# Revit family: 756-106-681-DN700-2800
name_source: partatom
category: Pipe Accessories
units: mm (PartAtom-declared; Revit-internal decimal feet)

## family parameters
Always vertical = Yes
Cut with Voids When Loaded = No
Part Type = Valve - Breaks Into
Round Connector Dimension = Use Diameter
Shared = No
Work Plane-Based = No

## types (27) — shared parameters
Body_wallthickness = 10 mm  [stored 0.0328084 ft]
DN0700_PN10 = 756-0700-1-04006
DN0700_PN16 = 756-0700-1-14006
DN0800_PN10 = 756-0800-1-04006
DN0800_PN16 = 756-0800-1-14006
DN0900_PN10 = 756-0900-1-04006
DN0900_PN16 = 756-0900-1-14006
DN1000 = Yes
DN1000_PN10 = 756-1000-1-04006
DN1000_PN16 = 756-1000-1-14006
DN1200 = Yes
DN1200_PN10 = 756-1200-1-04006
DN1200_PN16 = 756-1200-1-14006
DN1400 = Yes
DN1400_PN10 = 756-1400-1-04006
DN1400_PN16 = 756-1400-1-14006
DN1500 = Yes
DN1500_PN10 = 756-1500-1-04006
DN1500_PN16 = 756-1500-1-14006
DN1600 = Yes
DN1600_PN10 = 756-1600-1-04006
DN1600_PN16 = 756-1600-1-14006
DN1800 = Yes
DN1800_PN10 = 756-1800-1-04006
DN1800_PN16 = 756-1800-1-14006
DN2000 = Yes
DN2000_PN10 = 756-2000-1-04006
DN2000_PN16 = 756-2000-1-14006
DN2200 = Yes
DN2200_PN10_DIN = 756-2200-1-04006
DN2200_PN16_DIN = 756-2200-1-14006
DN2400 = Yes
DN2400_PN10_DIN = 756-2400-1-04006
DN2400_PN16_DIN = 756-2400-1-14006
DN2600 = Yes
DN2600_PN10 = 756-2600-1-04006
DN2600_PN16 = 756-2600-1-14006
DN2800 = Yes
DN2800_PN10 = 756-2800-1-04006
DN700 = Yes
DN800 = Yes
DN900 = Yes
Description_ = AVK_DOUBLE_ECCENTRIC_BUTTERFLY_VALVE
HW_rod_Dia = 30 mm  [stored 0.0984252 ft]
Offset = 3 mm  [stored 0.00984252 ft]
Pin_dia = 60 mm  [stored 0.19685 ft]
RF_Cut_Thickness = 5 mm  [stored 0.0164042 ft]
Rib_depth = 15 mm  [stored 0.0492126 ft]
Search_table = 756-106-681-DN700-2800
URL_product_pages = https://www.avkvalves.com

## per-type parameters (varying)
- DN0700_PN10: Bottom_Depth=1050 mm; Bottom_width=395 mm; CD_rod=39 mm  [stored 0.127953 ft]; D=285 mm; DN=700 mm; Disc_Dia=689 mm; Disc_width=40 mm  [stored 0.131234 ft]; Disk_1=40 mm  [stored 0.131234 ft]; Disk_2=40 mm  [stored 0.131234 ft]; Flange_OD=448 mm; Flange_Thickness=40 mm  [stored 0.131234 ft]; Gear_box_Mount_Flange_thickness=30 mm  [stored 0.0984252 ft]; Gear_box_Mount_Flange_width=102 mm; Gear_box_Mount_width=62 mm  [stored 0.203412 ft]; Gear_box_width=133 mm; H1=497 mm; H2=550 mm; HW_Connecting_Rib=570 mm; HW_Connecting_Rib_ref=569 mm; HW_Ref=110 mm; HW_height=381 mm; Hand_wheel_rod=33 mm  [stored 0.108268 ft]; ID (Radius)=350 mm; L=430 mm; L1=127 mm; L2=133 mm; Pin_Depth=798 mm; Pin_width=215 mm; Rf_Dia=397 mm; Rib_height=407 mm; Rib_height_2=50 mm  [stored 0.164042 ft]; Rib_width=350 mm; Rib_width_2=204 mm; W1=448 mm; W2=641 mm; W3=533 mm; W4=543 mm; W5=396 mm
- DN0700_PN16: Bottom_Depth=1050 mm; Bottom_width=427 mm; CD_rod=39 mm  [stored 0.127953 ft]; D=335 mm; DN=700 mm; Disc_Dia=689 mm; Disc_width=40 mm  [stored 0.131234 ft]; Disk_1=40 mm  [stored 0.131234 ft]; Disk_2=40 mm  [stored 0.131234 ft]; Flange_OD=455 mm; Flange_Thickness=40 mm  [stored 0.131234 ft]; Gear_box_Mount_Flange_thickness=30 mm  [stored 0.0984252 ft]; Gear_box_Mount_Flange_width=107 mm; Gear_box_Mount_width=66 mm  [stored 0.216535 ft]; Gear_box_width=139 mm; H1=532 mm; H2=550 mm; HW_Connecting_Rib=670 mm; HW_Connecting_Rib_ref=587 mm; HW_Ref=110 mm; HW_height=502 mm; Hand_wheel_rod=35 mm; ID (Radius)=350 mm; L=430 mm; L1=127 mm; L2=133 mm; Pin_Depth=805 mm; Pin_width=215 mm; Rf_Dia=397 mm; Rib_height=414 mm; Rib_height_2=77 mm  [stored 0.252625 ft]; Rib_width=350 mm; Rib_width_2=214 mm; W1=455 mm; W2=641 mm; W3=533 mm; W4=543 mm; W5=517 mm
- DN0800_PN10: Bottom_Depth=1200 mm; Bottom_width=460 mm; CD_rod=39 mm  [stored 0.127953 ft]; D=285 mm; DN=800 mm; Disc_Dia=788 mm; Disc_width=40 mm  [stored 0.131234 ft]; Disk_1=40 mm  [stored 0.131234 ft]; Disk_2=40 mm  [stored 0.131234 ft]; Flange_OD=508 mm; Flange_Thickness=40 mm  [stored 0.131234 ft]; Gear_box_Mount_Flange_thickness=40 mm  [stored 0.131234 ft]; Gear_box_Mount_Flange_width=112 mm; Gear_box_Mount_width=68 mm  [stored 0.223097 ft]; Gear_box_width=145 mm; H1=603 mm; H2=620 mm; HW_Connecting_Rib=570 mm; HW_Connecting_Rib_ref=657 mm; HW_Ref=125 mm; HW_height=381 mm; Hand_wheel_rod=36 mm  [stored 0.11811 ft]; ID (Radius)=400 mm; L=470 mm; L1=156 mm; L2=162 mm; Pin_Depth=908 mm; Pin_width=235 mm; Rf_Dia=450 mm; Rib_height=461 mm; Rib_height_2=96 mm; Rib_width=390 mm; Rib_width_2=223 mm; W1=508 mm; W2=711 mm; W3=627 mm; W4=636 mm; W5=396 mm
- DN0800_PN16: Bottom_Depth=1200 mm; Bottom_width=492 mm; CD_rod=39 mm  [stored 0.127953 ft]; D=335 mm; DN=800 mm; Disc_Dia=788 mm; Disc_width=40 mm  [stored 0.131234 ft]; Disk_1=40 mm  [stored 0.131234 ft]; Disk_2=40 mm  [stored 0.131234 ft]; Flange_OD=513 mm; Flange_Thickness=40 mm  [stored 0.131234 ft]; Gear_box_Mount_Flange_thickness=40 mm  [stored 0.131234 ft]; Gear_box_Mount_Flange_width=116 mm; Gear_box_Mount_width=72 mm  [stored 0.23622 ft]; Gear_box_width=151 mm; H1=603 mm; H2=620 mm; HW_Connecting_Rib=670 mm; HW_Connecting_Rib_ref=657 mm; HW_Ref=125 mm; HW_height=502 mm; Hand_wheel_rod=38 mm  [stored 0.124672 ft]; ID (Radius)=400 mm; L=470 mm; L1=156 mm; L2=162 mm; Pin_Depth=913 mm; Pin_width=235 mm; Rf_Dia=450 mm; Rib_height=466 mm; Rib_height_2=91 mm; Rib_width=390 mm; Rib_width_2=232 mm; W1=513 mm; W2=711 mm; W3=627 mm; W4=636 mm; W5=517 mm
- DN0900_PN10: Bottom_Depth=1350 mm; Bottom_width=524 mm; CD_rod=39 mm  [stored 0.127953 ft]; D=335 mm; DN=900 mm; Disc_Dia=888 mm; Disc_width=40 mm  [stored 0.131234 ft]; Disk_1=40 mm  [stored 0.131234 ft]; Disk_2=40 mm  [stored 0.131234 ft]; Flange_OD=558 mm; Flange_Thickness=40 mm  [stored 0.131234 ft]; Gear_box_Mount_Flange_thickness=40 mm  [stored 0.131234 ft]; Gear_box_Mount_Flange_width=121 mm; Gear_box_Mount_width=74 mm  [stored 0.242782 ft]; Gear_box_width=157 mm; H1=674 mm; H2=690 mm; HW_Connecting_Rib=670 mm; HW_Connecting_Rib_ref=733 mm; HW_Ref=128 mm; HW_height=502 mm; Hand_wheel_rod=39 mm  [stored 0.127953 ft]; ID (Radius)=450 mm; L=510 mm; L1=186 mm; L2=192 mm; Pin_Depth=1008 mm; Pin_width=255 mm; Rf_Dia=500 mm; Rib_height=507 mm; Rib_height_2=117 mm; Rib_width=430 mm; Rib_width_2=241 mm; W1=558 mm; W2=791 mm; W3=722 mm; W4=730 mm; W5=517 mm
- DN0900_PN16: Bottom_Depth=1350 mm; Bottom_width=556 mm; CD_rod=39 mm  [stored 0.127953 ft]; D=335 mm; DN=900 mm; Disc_Dia=888 mm; Disc_width=40 mm  [stored 0.131234 ft]; Disk_1=40 mm  [stored 0.131234 ft]; Disk_2=40 mm  [stored 0.131234 ft]; Flange_OD=563 mm; Flange_Thickness=40 mm  [stored 0.131234 ft]; Gear_box_Mount_Flange_thickness=40 mm  [stored 0.131234 ft]; Gear_box_Mount_Flange_width=125 mm; Gear_box_Mount_width=76 mm  [stored 0.249344 ft]; Gear_box_width=163 mm; H1=674 mm; H2=690 mm; HW_Connecting_Rib=670 mm; HW_Connecting_Rib_ref=733 mm; HW_Ref=128 mm; HW_height=555 mm; Hand_wheel_rod=41 mm  [stored 0.134514 ft]; ID (Radius)=450 mm; L=510 mm; L1=186 mm; L2=192 mm; Pin_Depth=1013 mm; Pin_width=255 mm; Rf_Dia=500 mm; Rib_height=511 mm; Rib_height_2=112 mm; Rib_width=430 mm; Rib_width_2=250 mm; W1=563 mm; W2=791 mm; W3=722 mm; W4=730 mm; W5=570 mm
- DN1000_PN10: Bottom_Depth=1500 mm; Bottom_width=588 mm; CD_rod=49 mm  [stored 0.160761 ft]; D=335 mm; DN=1000 mm; Disc_Dia=987 mm; Disc_width=50 mm  [stored 0.164042 ft]; Disk_1=40 mm  [stored 0.131234 ft]; Disk_2=40 mm  [stored 0.131234 ft]; Flange_OD=615 mm; Flange_Thickness=40 mm  [stored 0.131234 ft]; Gear_box_Mount_Flange_thickness=40 mm  [stored 0.131234 ft]; Gear_box_Mount_Flange_width=130 mm; Gear_box_Mount_width=80 mm; Gear_box_width=168 mm; H1=745 mm; H2=770 mm; HW_Connecting_Rib=670 mm; HW_Connecting_Rib_ref=808 mm; HW_Ref=130 mm; HW_height=515 mm; Hand_wheel_rod=42 mm  [stored 0.137795 ft]; ID (Radius)=500 mm; L=550 mm; L1=216 mm; L2=222 mm; Pin_Depth=1115 mm; Pin_width=275 mm; Rf_Dia=556 mm; Rib_height=559 mm; Rib_height_2=130 mm; Rib_width=470 mm; Rib_width_2=259 mm; W1=615 mm; W2=871 mm; W3=816 mm; W4=824 mm; W5=530 mm
- DN1000_PN16: Bottom_Depth=1500 mm; Bottom_width=620 mm; CD_rod=49 mm  [stored 0.160761 ft]; D=285 mm; DN=1000 mm; Disc_Dia=987 mm; Disc_width=50 mm  [stored 0.164042 ft]; Disk_1=50 mm  [stored 0.164042 ft]; Disk_2=50 mm  [stored 0.164042 ft]; Flange_OD=628 mm; Flange_Thickness=40 mm  [stored 0.131234 ft]; Gear_box_Mount_Flange_thickness=40 mm  [stored 0.131234 ft]; Gear_box_Mount_Flange_width=134 mm; Gear_box_Mount_width=82 mm; Gear_box_width=174 mm; H1=745 mm; H2=770 mm; HW_Connecting_Rib=570 mm; HW_Connecting_Rib_ref=808 mm; HW_Ref=130 mm; HW_height=555 mm; Hand_wheel_rod=44 mm; ID (Radius)=500 mm; L=550 mm; L1=216 mm; L2=222 mm; Pin_Depth=1128 mm; Pin_width=275 mm; Rf_Dia=556 mm; Rib_height=570 mm; Rib_height_2=118 mm; Rib_width=470 mm; Rib_width_2=268 mm; W1=628 mm; W2=871 mm; W3=816 mm; W4=824 mm; W5=570 mm
- DN1200_PN10: Bottom_Depth=1800 mm; Bottom_width=653 mm; CD_rod=49 mm  [stored 0.160761 ft]; D=285 mm; DN=1200 mm; Disc_Dia=1174 mm; Disc_width=50 mm  [stored 0.164042 ft]; Disk_1=50 mm  [stored 0.164042 ft]; Disk_2=50 mm  [stored 0.164042 ft]; Flange_OD=728 mm; Flange_Thickness=40 mm  [stored 0.131234 ft]; Gear_box_Mount_Flange_thickness=40 mm  [stored 0.131234 ft]; Gear_box_Mount_Flange_width=139 mm; Gear_box_Mount_width=84 mm; Gear_box_width=180 mm; H1=840 mm; H2=855 mm; HW_Connecting_Rib=570 mm; HW_Connecting_Rib_ref=898 mm; HW_Ref=128 mm; HW_height=555 mm; Hand_wheel_rod=45 mm  [stored 0.147638 ft]; ID (Radius)=600 mm; L=630 mm; L1=269 mm; L2=275 mm; Pin_Depth=1328 mm; Pin_width=315 mm; Rf_Dia=666 mm; Rib_height=661 mm; Rib_height_2=113 mm; Rib_width=550 mm; Rib_width_2=277 mm; W1=728 mm; W2=956 mm; W3=986 mm; W4=993 mm; W5=570 mm
- DN1200_PN16: Bottom_Depth=1800 mm; Bottom_width=685 mm; CD_rod=49 mm  [stored 0.160761 ft]; D=335 mm; DN=1200 mm; Disc_Dia=1174 mm; Disc_width=50 mm  [stored 0.164042 ft]; Disk_1=50 mm  [stored 0.164042 ft]; Disk_2=50 mm  [stored 0.164042 ft]; Flange_OD=743 mm; Flange_Thickness=50 mm  [stored 0.164042 ft]; Gear_box_Mount_Flange_thickness=40 mm  [stored 0.131234 ft]; Gear_box_Mount_Flange_width=143 mm; Gear_box_Mount_width=88 mm; Gear_box_width=186 mm; H1=840 mm; H2=855 mm; HW_Connecting_Rib=670 mm; HW_Connecting_Rib_ref=898 mm; HW_Ref=128 mm; HW_height=576 mm; Hand_wheel_rod=47 mm  [stored 0.154199 ft]; ID (Radius)=600 mm; L=630 mm; L1=269 mm; L2=275 mm; Pin_Depth=1343 mm; Pin_width=315 mm; Rf_Dia=666 mm; Rib_height=675 mm; Rib_height_2=98 mm; Rib_width=530 mm; Rib_width_2=286 mm; W1=743 mm; W2=956 mm; W3=986 mm; W4=993 mm; W5=591 mm
- DN1400_PN10: Bottom_Depth=2100 mm; Bottom_width=717 mm; CD_rod=59 mm  [stored 0.19357 ft]; D=335 mm; DN=1400 mm; Disc_Dia=1381 mm; Disc_width=60 mm  [stored 0.19685 ft]; Disk_1=50 mm  [stored 0.164042 ft]; Disk_2=50 mm  [stored 0.164042 ft]; Flange_OD=838 mm; Flange_Thickness=50 mm  [stored 0.164042 ft]; Gear_box_Mount_Flange_thickness=40 mm  [stored 0.131234 ft]; Gear_box_Mount_Flange_width=148 mm; Gear_box_Mount_width=90 mm; Gear_box_width=192 mm; H1=920 mm; H2=970 mm; HW_Connecting_Rib=670 mm; HW_Connecting_Rib_ref=996 mm; HW_Ref=150 mm; HW_height=555 mm; Hand_wheel_rod=48 mm  [stored 0.15748 ft]; ID (Radius)=700 mm; L=710 mm; L1=333 mm; L2=339 mm; Pin_Depth=1538 mm; Pin_width=355 mm; Rf_Dia=763 mm; Rib_height=761 mm; Rib_height_2=83 mm; Rib_width=610 mm; Rib_width_2=295 mm; W1=838 mm; W2=1071 mm; W3=1182 mm; W4=1189 mm; W5=570 mm
- DN1400_PN16: Bottom_Depth=2100 mm; Bottom_width=749 mm; CD_rod=59 mm  [stored 0.19357 ft]; D=335 mm; DN=1400 mm; Disc_Dia=1381 mm; Disc_width=60 mm  [stored 0.19685 ft]; Disk_1=50 mm  [stored 0.164042 ft]; Disk_2=50 mm  [stored 0.164042 ft]; Flange_OD=843 mm; Flange_Thickness=50 mm  [stored 0.164042 ft]; Gear_box_Mount_Flange_thickness=40 mm  [stored 0.131234 ft]; Gear_box_Mount_Flange_width=152 mm; Gear_box_Mount_width=94 mm; Gear_box_width=198 mm; H1=920 mm; H2=970 mm; HW_Connecting_Rib=670 mm; HW_Connecting_Rib_ref=1020 mm; HW_Ref=150 mm; HW_height=576 mm; Hand_wheel_rod=50 mm  [stored 0.164042 ft]; ID (Radius)=700 mm; L=710 mm; L1=333 mm; L2=339 mm; Pin_Depth=1543 mm; Pin_width=355 mm; Rf_Dia=763 mm; Rib_height=766 mm; Rib_height_2=78 mm; Rib_width=610 mm; Rib_width_2=304 mm; W1=843 mm; W2=1119 mm; W3=1182 mm; W4=1189 mm; W5=591 mm
- DN1500_PN10: Bottom_Depth=2250 mm; Bottom_width=781 mm; CD_rod=59 mm  [stored 0.19357 ft]; D=335 mm; DN=1500 mm; Disc_Dia=1481 mm; Disc_width=60 mm  [stored 0.19685 ft]; Disk_1=50 mm  [stored 0.164042 ft]; Disk_2=50 mm  [stored 0.164042 ft]; Flange_OD=893 mm; Flange_Thickness=50 mm  [stored 0.164042 ft]; Gear_box_Mount_Flange_thickness=40 mm  [stored 0.131234 ft]; Gear_box_Mount_Flange_width=157 mm; Gear_box_Mount_width=96 mm; Gear_box_width=203 mm; H1=1000 mm; H2=1070 mm; HW_Connecting_Rib=670 mm; HW_Connecting_Rib_ref=1086 mm; HW_Ref=175 mm; HW_height=555 mm; Hand_wheel_rod=51 mm  [stored 0.167323 ft]; ID (Radius)=750 mm; L=750 mm; L1=363 mm; L2=369 mm; Pin_Depth=1643 mm; Pin_width=375 mm; Rf_Dia=818 mm; Rib_height=811 mm; Rib_height_2=108 mm; Rib_width=650 mm; Rib_width_2=313 mm; W1=893 mm; W2=1171 mm; W3=1274 mm; W4=1281 mm; W5=570 mm
- DN1500_PN16: Bottom_Depth=2250 mm; Bottom_width=813 mm; CD_rod=59 mm  [stored 0.19357 ft]; D=335 mm; DN=1500 mm; Disc_Dia=1481 mm; Disc_width=60 mm  [stored 0.19685 ft]; Disk_1=50 mm  [stored 0.164042 ft]; Disk_2=50 mm  [stored 0.164042 ft]; Flange_OD=910 mm; Flange_Thickness=50 mm  [stored 0.164042 ft]; Gear_box_Mount_Flange_thickness=50 mm  [stored 0.164042 ft]; Gear_box_Mount_Flange_width=162 mm; Gear_box_Mount_width=98 mm; Gear_box_width=210 mm; H1=1000 mm; H2=1070 mm; HW_Connecting_Rib=670 mm; HW_Connecting_Rib_ref=1110 mm; HW_Ref=175 mm; HW_height=576 mm; Hand_wheel_rod=53 mm  [stored 0.173885 ft]; ID (Radius)=750 mm; L=750 mm; L1=363 mm; L2=369 mm; Pin_Depth=1660 mm; Pin_width=375 mm; Rf_Dia=818 mm; Rib_height=827 mm; Rib_height_2=90 mm; Rib_width=650 mm; Rib_width_2=323 mm; W1=913 mm; W2=1219 mm; W3=1274 mm; W4=1281 mm; W5=591 mm
- DN1600_PN16: Bottom_Depth=2400 mm; Bottom_width=878 mm; CD_rod=69 mm  [stored 0.226378 ft]; D=335 mm; DN=1600 mm; Disc_Dia=1575 mm; Disc_width=70 mm  [stored 0.229659 ft]; Disk_1=50 mm  [stored 0.164042 ft]; Disk_2=50 mm  [stored 0.164042 ft]; Flange_OD=965 mm; Flange_Thickness=60 mm  [stored 0.19685 ft]; Gear_box_Mount_Flange_thickness=50 mm  [stored 0.164042 ft]; Gear_box_Mount_Flange_width=171 mm; Gear_box_Mount_width=104 mm; Gear_box_width=222 mm; H1=1090 mm; H2=1145 mm; HW_Connecting_Rib=670 mm; HW_Connecting_Rib_ref=1192 mm; HW_Ref=181 mm; HW_height=616 mm; Hand_wheel_rod=56 mm  [stored 0.183727 ft]; ID (Radius)=800 mm; L=790 mm; L1=390 mm; L2=396 mm; Pin_Depth=1765 mm; Pin_width=395 mm; Rf_Dia=875 mm; Rib_height=877 mm; Rib_height_2=125 mm; Rib_width=670 mm; Rib_width_2=341 mm; W1=965 mm; W2=1294 mm; W3=1359 mm; W4=1366 mm; W5=631 mm
- DN1600_PN10: Bottom_Depth=2400 mm; Bottom_width=846 mm; CD_rod=69 mm  [stored 0.226378 ft]; D=335 mm; DN=1600 mm; Disc_Dia=1575 mm; Disc_width=70 mm  [stored 0.229659 ft]; Disk_1=50 mm  [stored 0.164042 ft]; Disk_2=50 mm  [stored 0.164042 ft]; Flange_OD=958 mm; Flange_Thickness=50 mm  [stored 0.164042 ft]; Gear_box_Mount_Flange_thickness=50 mm  [stored 0.164042 ft]; Gear_box_Mount_Flange_width=166 mm; Gear_box_Mount_width=102 mm; Gear_box_width=216 mm; H1=1090 mm; H2=1145 mm; HW_Connecting_Rib=670 mm; HW_Connecting_Rib_ref=1192 mm; HW_Ref=181 mm; HW_height=576 mm; Hand_wheel_rod=54 mm  [stored 0.177165 ft]; ID (Radius)=800 mm; L=790 mm; L1=390 mm; L2=396 mm; Pin_Depth=1758 mm; Pin_width=395 mm; Rf_Dia=875 mm; Rib_height=870 mm; Rib_height_2=133 mm; Rib_width=690 mm; Rib_width_2=332 mm; W1=958 mm; W2=1294 mm; W3=1359 mm; W4=1366 mm; W5=591 mm
- DN1800_PN16: Bottom_Depth=2700 mm; Bottom_width=942 mm; CD_rod=69 mm  [stored 0.226378 ft]; D=335 mm; DN=1800 mm; Disc_Dia=1771 mm; Disc_width=70 mm  [stored 0.229659 ft]; Disk_1=50 mm  [stored 0.164042 ft]; Disk_2=50 mm  [stored 0.164042 ft]; Flange_OD=1065 mm; Flange_Thickness=60 mm  [stored 0.19685 ft]; Gear_box_Mount_Flange_thickness=50 mm  [stored 0.164042 ft]; Gear_box_Mount_Flange_width=180 mm; Gear_box_Mount_width=110 mm; Gear_box_width=233 mm; H1=1180 mm; H2=1220 mm; HW_Connecting_Rib=670 mm; HW_Connecting_Rib_ref=1289 mm; HW_Ref=170 mm; HW_height=706 mm; Hand_wheel_rod=59 mm  [stored 0.19357 ft]; ID (Radius)=900 mm; L=870 mm; L1=448 mm; L2=454 mm; Pin_Depth=1965 mm; Pin_width=435 mm; Rf_Dia=973 mm; Rib_height=968 mm; Rib_height_2=115 mm; Rib_width=750 mm; Rib_width_2=359 mm; W1=1065 mm; W2=1398 mm; W3=1540 mm; W4=1547 mm; W5=721 mm
- DN1800_PN10: Bottom_Depth=2700 mm; Bottom_width=910 mm; CD_rod=69 mm  [stored 0.226378 ft]; D=335 mm; DN=1800 mm; Disc_Dia=1771 mm; Disc_width=70 mm  [stored 0.229659 ft]; Disk_1=50 mm  [stored 0.164042 ft]; Disk_2=50 mm  [stored 0.164042 ft]; Flange_OD=1058 mm; Flange_Thickness=60 mm  [stored 0.19685 ft]; Gear_box_Mount_Flange_thickness=50 mm  [stored 0.164042 ft]; Gear_box_Mount_Flange_width=175 mm; Gear_box_Mount_width=106 mm; Gear_box_width=228 mm; H1=1180 mm; H2=1220 mm; HW_Connecting_Rib=670 mm; HW_Connecting_Rib_ref=1275 mm; HW_Ref=170 mm; HW_height=616 mm; Hand_wheel_rod=57 mm  [stored 0.187008 ft]; ID (Radius)=900 mm; L=870 mm; L1=448 mm; L2=454 mm; Pin_Depth=1958 mm; Pin_width=435 mm; Rf_Dia=973 mm; Rib_height=961 mm; Rib_height_2=123 mm; Rib_width=750 mm; Rib_width_2=350 mm; W1=1058 mm; W2=1369 mm; W3=1540 mm; W4=1547 mm; W5=631 mm
- DN2000_PN10: Bottom_Depth=3000 mm; Bottom_width=974 mm; CD_rod=79 mm; D=335 mm; DN=2000 mm; Disc_Dia=1997 mm; Disc_width=80 mm; Disk_1=50 mm  [stored 0.164042 ft]; Disk_2=50 mm  [stored 0.164042 ft]; Flange_OD=1163 mm; Flange_Thickness=60 mm  [stored 0.19685 ft]; Gear_box_Mount_Flange_thickness=50 mm  [stored 0.164042 ft]; Gear_box_Mount_Flange_width=184 mm; Gear_box_Mount_width=112 mm; Gear_box_width=239 mm; H1=1330 mm; H2=1382 mm; HW_Connecting_Rib=670 mm; HW_Connecting_Rib_ref=1439 mm; HW_Ref=191 mm; HW_height=671 mm; Hand_wheel_rod=60 mm  [stored 0.19685 ft]; ID (Radius)=1000 mm; L=950 mm; L1=521 mm; L2=527 mm; Pin_Depth=2163 mm; Pin_width=475 mm; Rf_Dia=1114 mm; Rib_height=1057 mm; Rib_height_2=168 mm; Rib_width=830 mm; Rib_width_2=368 mm; W1=1180 mm; W2=1547 mm; W3=1753 mm; W4=1760 mm; W5=686 mm
- DN2000_PN16: Bottom_Depth=3000 mm; Bottom_width=1006 mm; CD_rod=79 mm; D=335 mm; DN=2000 mm; Disc_Dia=1997 mm; Disc_width=80 mm; Disk_1=50 mm  [stored 0.164042 ft]; Disk_2=50 mm  [stored 0.164042 ft]; Flange_OD=1173 mm; Flange_Thickness=60 mm  [stored 0.19685 ft]; Gear_box_Mount_Flange_thickness=50 mm  [stored 0.164042 ft]; Gear_box_Mount_Flange_width=189 mm; Gear_box_Mount_width=116 mm; Gear_box_width=245 mm; H1=1330 mm; H2=1382 mm; HW_Connecting_Rib=670 mm; HW_Connecting_Rib_ref=1445 mm; HW_Ref=191 mm; HW_height=732 mm; Hand_wheel_rod=62 mm  [stored 0.203412 ft]; ID (Radius)=1000 mm; L=950 mm; L1=521 mm; L2=527 mm; Pin_Depth=2173 mm; Pin_width=475 mm; Rf_Dia=1114 mm; Rib_height=1066 mm; Rib_height_2=158 mm; Rib_width=830 mm; Rib_width_2=377 mm; W1=1180 mm; W2=1560 mm; W3=1753 mm; W4=1760 mm; W5=747 mm
- DN2200_PN16: Bottom_Depth=3300 mm; Bottom_width=1000 mm; CD_rod=79 mm; D=335 mm; DN=2200 mm; Disc_Dia=2187 mm; Disc_width=80 mm; Disk_1=60 mm  [stored 0.19685 ft]; Disk_2=60 mm  [stored 0.19685 ft]; Flange_OD=1278 mm; Flange_Thickness=60 mm  [stored 0.19685 ft]; Gear_box_Mount_Flange_thickness=50 mm  [stored 0.164042 ft]; Gear_box_Mount_Flange_width=198 mm; Gear_box_Mount_width=120 mm; Gear_box_width=257 mm; H1=1410 mm; H2=1482 mm; HW_Connecting_Rib=670 mm; HW_Connecting_Rib_ref=1526 mm; HW_Ref=170 mm; HW_height=749 mm; Hand_wheel_rod=65 mm; ID (Radius)=1100 mm; L=1030 mm; L1=576 mm; L2=582 mm; Pin_Depth=2378 mm; Pin_width=515 mm; Rf_Dia=1180 mm; Rib_height=1161 mm; Rib_height_2=133 mm; Rib_width=910 mm; Rib_width_2=395 mm; W1=1278 mm; W2=1641 mm; W3=1926 mm; W4=1932 mm; W5=764 mm
- DN2200_PN10: Bottom_Depth=3300 mm; Bottom_width=1000 mm; CD_rod=79 mm; D=335 mm; DN=2200 mm; Disc_Dia=2187 mm; Disc_width=80 mm; Disk_1=50 mm  [stored 0.164042 ft]; Disk_2=50 mm  [stored 0.164042 ft]; Flange_OD=1275 mm; Flange_Thickness=60 mm  [stored 0.19685 ft]; Gear_box_Mount_Flange_thickness=50 mm  [stored 0.164042 ft]; Gear_box_Mount_Flange_width=193 mm; Gear_box_Mount_width=118 mm; Gear_box_width=251 mm; H1=1410 mm; H2=1472 mm; HW_Connecting_Rib=670 mm; HW_Connecting_Rib_ref=1530 mm; HW_Ref=170 mm; HW_height=706 mm; Hand_wheel_rod=63 mm  [stored 0.206693 ft]; ID (Radius)=1100 mm; L=1030 mm; L1=576 mm; L2=582 mm; Pin_Depth=2375 mm; Pin_width=515 mm; Rf_Dia=1180 mm; Rib_height=1159 mm; Rib_height_2=135 mm; Rib_width=910 mm; Rib_width_2=386 mm; W1=1275 mm; W2=1650 mm; W3=1926 mm; W4=1932 mm; W5=721 mm
- DN2600_PN16: Bottom_Depth=3900 mm; Bottom_width=1199 mm; CD_rod=99 mm; D=185 mm; DN=2600 mm; Disc_Dia=2582 mm; Disc_width=100 mm; Disk_1=60 mm  [stored 0.19685 ft]; Disk_2=60 mm  [stored 0.19685 ft]; Flange_OD=1524 mm; Flange_Thickness=70 mm  [stored 0.229659 ft]; Gear_box_Mount_Flange_thickness=50 mm  [stored 0.164042 ft]; Gear_box_Mount_Flange_width=216 mm; Gear_box_Mount_width=132 mm; Gear_box_width=281 mm; H1=1740 mm; H2=1855 mm; HW_Connecting_Rib=370 mm; HW_Connecting_Rib_ref=1895 mm; HW_Ref=214 mm; HW_height=765 mm; Hand_wheel_rod=71 mm; ID (Radius)=1300 mm; L=1190 mm; L1=693 mm; L2=699 mm; Pin_Depth=2824 mm; Pin_width=595 mm; Rf_Dia=1415 mm; Rib_height=1385 mm; Rib_height_2=216 mm; Rib_width=1050 mm; Rib_width_2=432 mm; W1=1535 mm; W2=2050 mm; W3=2289 mm; W4=2295 mm; W5=780 mm
- DN2600_PN10: Bottom_Depth=3900 mm; Bottom_width=1167 mm; CD_rod=99 mm; D=185 mm; DN=2600 mm; Disc_Dia=2582 mm; Disc_width=100 mm; Disk_1=60 mm  [stored 0.19685 ft]; Disk_2=60 mm  [stored 0.19685 ft]; Flange_OD=1480 mm; Flange_Thickness=70 mm  [stored 0.229659 ft]; Gear_box_Mount_Flange_thickness=50 mm  [stored 0.164042 ft]; Gear_box_Mount_Flange_width=211 mm; Gear_box_Mount_width=128 mm; Gear_box_width=274 mm; H1=1740 mm; H2=1820 mm; HW_Connecting_Rib=370 mm; HW_Connecting_Rib_ref=1875 mm; HW_Ref=214 mm; HW_height=765 mm; Hand_wheel_rod=69 mm  [stored 0.226378 ft]; ID (Radius)=1300 mm; L=1190 mm; L1=693 mm; L2=699 mm; Pin_Depth=2780 mm; Pin_width=595 mm; Rf_Dia=1415 mm; Rib_height=1345 mm; Rib_height_2=260 mm; Rib_width=1050 mm; Rib_width_2=422 mm; W1=1490 mm; W2=2010 mm; W3=2289 mm; W4=2295 mm; W5=780 mm
- DN2400_PN10: Bottom_Depth=3600 mm; Bottom_width=1103 mm; CD_rod=89 mm; D=335 mm; DN=2400 mm; Disc_Dia=2382 mm; Disc_width=90 mm; Disk_1=60 mm  [stored 0.19685 ft]; Disk_2=60 mm  [stored 0.19685 ft]; Flange_OD=1380 mm; Flange_Thickness=70 mm  [stored 0.229659 ft]; Gear_box_Mount_Flange_thickness=50 mm  [stored 0.164042 ft]; Gear_box_Mount_Flange_width=202 mm; Gear_box_Mount_width=124 mm; Gear_box_width=263 mm; H1=1570 mm; H2=1613 mm; HW_Connecting_Rib=670 mm; HW_Connecting_Rib_ref=1665 mm; HW_Ref=168 mm; HW_height=737 mm; Hand_wheel_rod=66 mm  [stored 0.216535 ft]; ID (Radius)=1200 mm; L=1110 mm; L1=633 mm; L2=639 mm; Pin_Depth=2580 mm; Pin_width=555 mm; Rf_Dia=1273 mm; Rib_height=1255 mm; Rib_height_2=190 mm; Rib_width=970 mm; Rib_width_2=404 mm; W1=1380 mm; W2=1759 mm; W3=2103 mm; W4=2019 mm; W5=752 mm
- DN2400_PN16: Bottom_Depth=3600 mm; Bottom_width=1135 mm; CD_rod=89 mm; D=335 mm; DN=2400 mm; Disc_Dia=2382 mm; Disc_width=90 mm; Disk_1=60 mm  [stored 0.19685 ft]; Disk_2=60 mm  [stored 0.19685 ft]; Flange_OD=1383 mm; Flange_Thickness=70 mm  [stored 0.229659 ft]; Gear_box_Mount_Flange_thickness=50 mm  [stored 0.164042 ft]; Gear_box_Mount_Flange_width=207 mm; Gear_box_Mount_width=126 mm; Gear_box_width=268 mm; H1=1570 mm; H2=1584 mm; HW_Connecting_Rib=670 mm; HW_Connecting_Rib_ref=1662 mm; HW_Ref=168 mm; HW_height=749 mm; Hand_wheel_rod=68 mm  [stored 0.223097 ft]; ID (Radius)=1200 mm; L=1110 mm; L1=676 mm; L2=682 mm; Pin_Depth=2583 mm; Pin_width=555 mm; Rf_Dia=1273 mm; Rib_height=1257 mm; Rib_height_2=188 mm; Rib_width=970 mm; Rib_width_2=413 mm; W1=1382 mm; W2=1753 mm; W3=2126 mm; W4=2132 mm; W5=764 mm
- DN2800_PN10: Bottom_Depth=4200 mm; Bottom_width=1232 mm; CD_rod=99 mm; D=285 mm; DN=2800 mm; Disc_Dia=2752 mm; Disc_width=100 mm; Disk_1=60 mm  [stored 0.19685 ft]; Disk_2=60 mm  [stored 0.19685 ft]; Flange_OD=1590 mm; Flange_Thickness=70 mm  [stored 0.229659 ft]; Gear_box_Mount_Flange_thickness=50 mm  [stored 0.164042 ft]; Gear_box_Mount_Flange_width=221 mm; Gear_box_Mount_width=134 mm; Gear_box_width=287 mm; H1=1820 mm; H2=1921 mm; HW_Connecting_Rib=570 mm; HW_Connecting_Rib_ref=1980 mm; HW_Ref=240 mm; HW_height=810 mm; Hand_wheel_rod=72 mm  [stored 0.23622 ft]; ID (Radius)=1400 mm; L=1270 mm; L1=738 mm; L2=739 mm; Pin_Depth=2990 mm; Pin_width=635 mm; Rf_Dia=1500 mm; Rib_height=1445 mm; Rib_height_2=230 mm; Rib_width=1130 mm; Rib_width_2=441 mm; W1=1600 mm; W2=2140 mm; W3=2441 mm; W4=2442 mm; W5=825 mm

note: [stored X ft] marks values corroborated as IEEE doubles in the binary element streams (Revit-internal decimal feet)

## geometry (parser evidence)
native form markers: Sweep x4
no freeform markers — native parametric forms only
